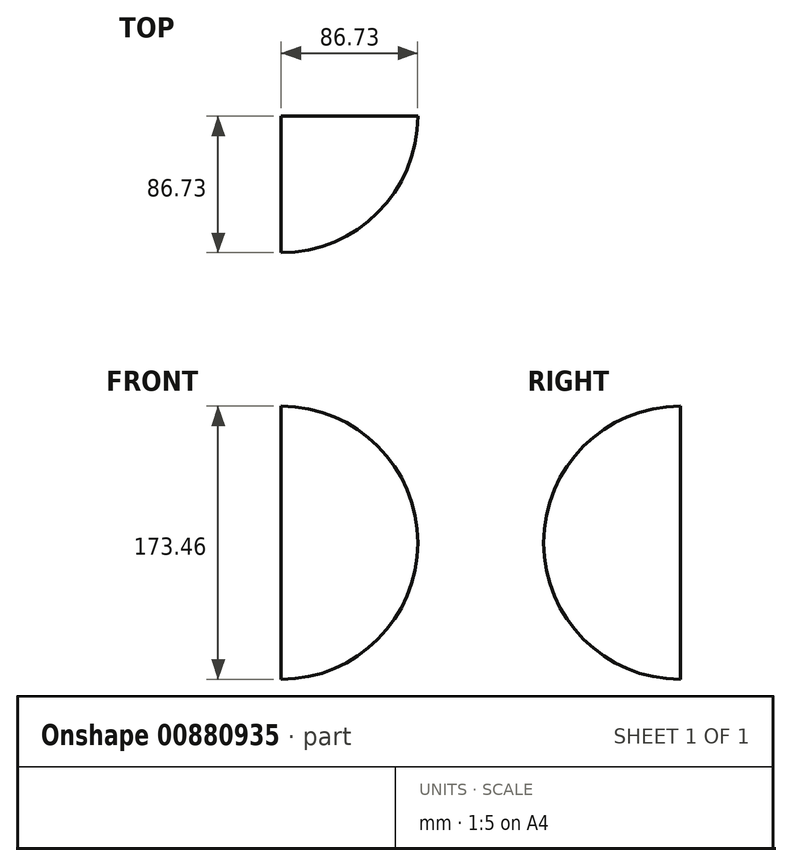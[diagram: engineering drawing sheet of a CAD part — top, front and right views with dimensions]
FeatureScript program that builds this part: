
annotation { "Feature Type Name" : "Feature", "Feature Type Description" : "" }
export const myFeature = defineFeature(function(context is Context, id is Id, definition is map)
    precondition{}
    {
        {
            var Q0;
            Q0=qCreatedBy(makeId("Front.planeOp"),FACE);
            var sketch = newSketch(context, id + "F0", { "sketchPlane" : qUnion([Q0])});
            skArc(sketch, "E0", {"start": v(0, -86.73) * mm, "mid": v(86.73, 0) * mm, "end": v(0, 86.73) * mm});
            skLineSegment(sketch, "E1", {"start": v(0, 86.73) * mm, "end": v(0, -86.73) * mm});
            skSolve(sketch);
        }
        {
            var Q0;
            Q0=sQuery(id+"F0.wireOp",EDGE,"E0");
            var Q1;
            Q1=sQuery(id+"F0.wireOp",EDGE,"E1");
            revolve(context, id + "F1", {"bodyType" : ToolBodyType.SURFACE, "surfaceOperationType" : NewSurfaceOperationType.NEW, "surfaceEntities" : qUnion([Q0]), "axis" : qUnion([Q1]), "revolveType" : RevolveType.ONE_DIRECTION, "angle" : 180 * degree});
        }
        {
            var Q0;
            Q0=makeQuery(id+"F0.imprint","IMPRINT",FACE,{"disambiguationData":[TD([[makeQuery(id+"F0.imprint","IMPRINT",EDGE,{"derivedFrom":sQuery(id+"F0.wireOp",EDGE,"E0")}),1.0]])]});
            extrude(context, id + "F2", {"entities" : qUnion([Q0]), "endBound" : BoundingType.UP_TO_NEXT, "depth" : 25 * mm, "offsetDistance" : 25 * mm});
        }
        {
            var Q0;
            Q0=sQuery(id+"F0.wireOp",EDGE,"E1");
            var Q1;
            Q1=sQuery(id+"F0.wireOp",EDGE,"E0");
            extrude(context, id + "F3", {"bodyType" : ToolBodyType.SURFACE, "surfaceEntities" : qUnion([Q0, Q1]), "oppositeDirection" : true, "depth" : 78 * mm, "offsetDistance" : 25 * mm});
        }
    });
